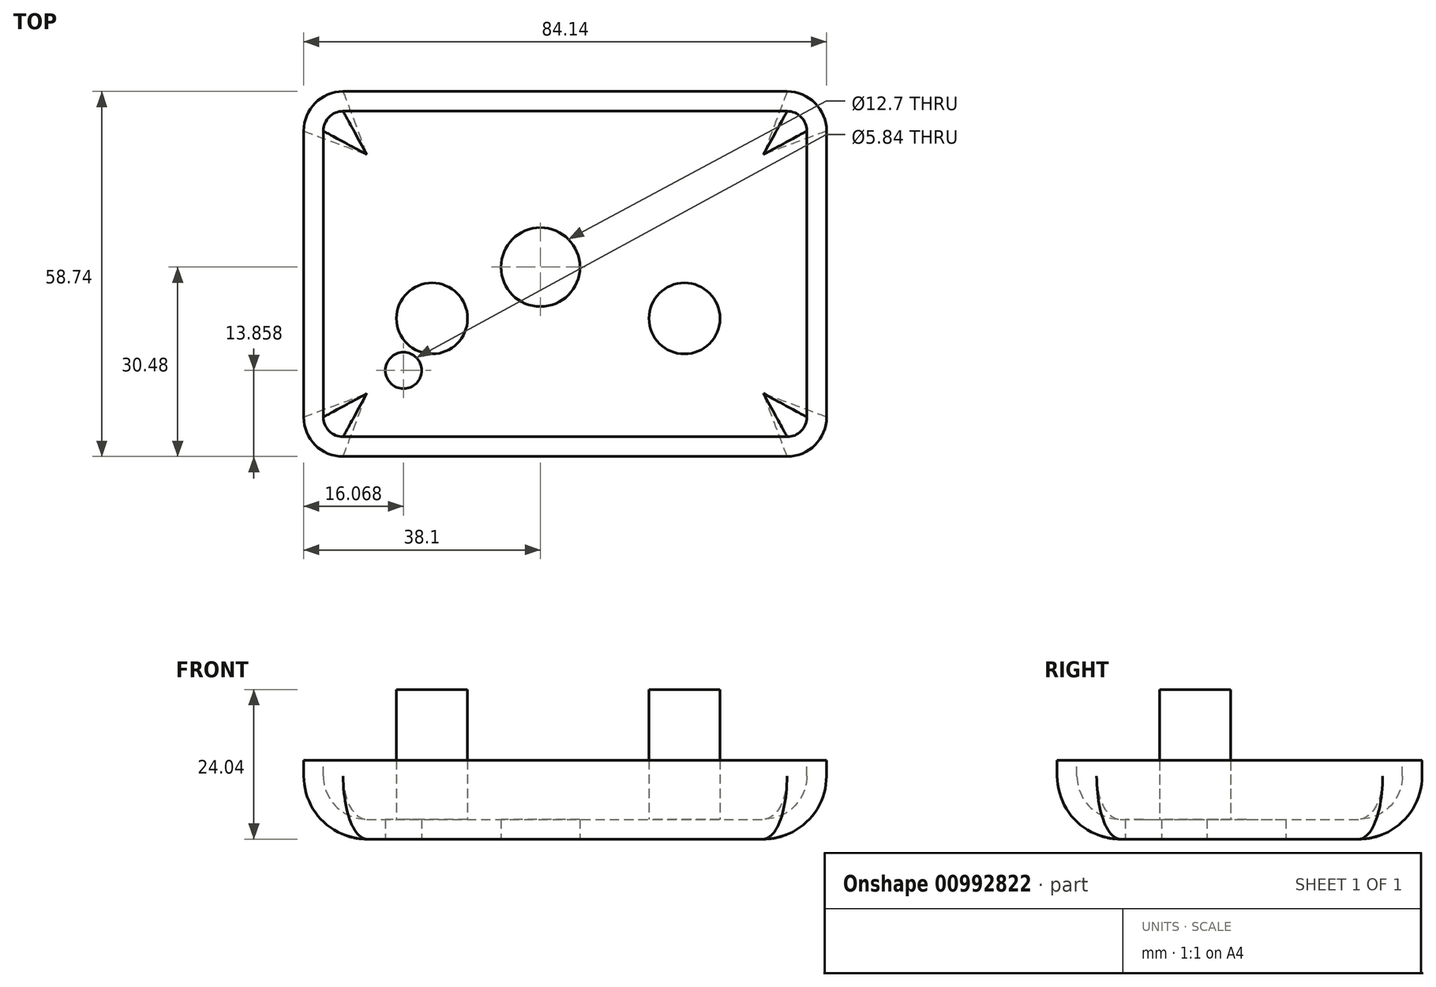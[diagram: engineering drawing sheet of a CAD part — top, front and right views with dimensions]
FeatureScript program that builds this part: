
annotation { "Feature Type Name" : "Feature", "Feature Type Description" : "" }
export const myFeature = defineFeature(function(context is Context, id is Id, definition is map)
    precondition{}
    {
        {
            var Q0;
            Q0=qCreatedBy(makeId("Top.planeOp"),FACE);
            var sketch = newSketch(context, id + "F0", { "sketchPlane" : qUnion([Q0])});
            skLineSegment(sketch, "E0.bottom", {"start": v(-31.75, 33.34) * mm, "end": v(39.69, 33.34) * mm});
            skLineSegment(sketch, "E0.top", {"start": v(-31.75, -25.4) * mm, "end": v(39.69, -25.4) * mm});
            skLineSegment(sketch, "E0.left", {"start": v(-38.1, 26.99) * mm, "end": v(-38.1, -19.05) * mm});
            skLineSegment(sketch, "E0.right", {"start": v(46.04, 26.99) * mm, "end": v(46.04, -19.05) * mm});
            skPoint(sketch, "E1.visualSharp", {"position": v(-38.1, -25.4) * mm});
            skArc(sketch, "E1.filletArc", {"start": v(-38.1, -19.05) * mm, "mid": v(-36.24, -23.54) * mm, "end": v(-31.75, -25.4) * mm});
            skPoint(sketch, "E2.visualSharp", {"position": v(-38.1, 33.34) * mm});
            skArc(sketch, "E2.filletArc", {"start": v(-31.75, 33.34) * mm, "mid": v(-36.24, 31.48) * mm, "end": v(-38.1, 26.99) * mm});
            skPoint(sketch, "E3.visualSharp", {"position": v(46.04, 33.34) * mm});
            skArc(sketch, "E3.filletArc", {"start": v(46.04, 26.99) * mm, "mid": v(44.18, 31.48) * mm, "end": v(39.69, 33.34) * mm});
            skPoint(sketch, "E4.visualSharp", {"position": v(46.04, -25.4) * mm});
            skArc(sketch, "E4.filletArc", {"start": v(39.69, -25.4) * mm, "mid": v(44.18, -23.54) * mm, "end": v(46.04, -19.05) * mm});
            skSolve(sketch);
        }
        {
            var Q0;
            Q0=makeQuery(id+"F0.imprint","IMPRINT",FACE,{"disambiguationData":[TD([[makeQuery(id+"F0.imprint","IMPRINT",EDGE,{"derivedFrom":sQuery(id+"F0.wireOp",EDGE,"E0.bottom")}),-1.0]])]});
            extrude(context, id + "F1", {"entities" : qUnion([Q0]), "oppositeDirection" : true, "depth" : 12.7 * mm, "offsetDistance" : 25.4 * mm});
        }
        {
            var Q0;
            Q0=makeQuery(id+"F1.opExtrude","CAP_EDGE",EDGE,{"disambiguationData":[OSD([sQuery(id+"F0.wireOp",EDGE,"E0.top")])],"isStart":false});
            var Q1;
            Q1=makeQuery(id+"F1.opExtrude","CAP_EDGE",EDGE,{"disambiguationData":[OSD([sQuery(id+"F0.wireOp",EDGE,"E1.filletArc")])],"isStart":false});
            var Q2;
            Q2=makeQuery(id+"F1.opExtrude","CAP_EDGE",EDGE,{"disambiguationData":[OSD([sQuery(id+"F0.wireOp",EDGE,"E0.left")])],"isStart":false});
            var Q3;
            Q3=makeQuery(id+"F1.opExtrude","CAP_EDGE",EDGE,{"disambiguationData":[OSD([sQuery(id+"F0.wireOp",EDGE,"E2.filletArc")])],"isStart":false});
            var Q4;
            Q4=makeQuery(id+"F1.opExtrude","CAP_EDGE",EDGE,{"disambiguationData":[OSD([sQuery(id+"F0.wireOp",EDGE,"E0.bottom")])],"isStart":false});
            var Q5;
            Q5=makeQuery(id+"F1.opExtrude","CAP_EDGE",EDGE,{"disambiguationData":[OSD([sQuery(id+"F0.wireOp",EDGE,"E3.filletArc")])],"isStart":false});
            var Q6;
            Q6=makeQuery(id+"F1.opExtrude","CAP_EDGE",EDGE,{"disambiguationData":[OSD([sQuery(id+"F0.wireOp",EDGE,"E0.right")])],"isStart":false});
            var Q7;
            Q7=makeQuery(id+"F1.opExtrude","CAP_EDGE",EDGE,{"disambiguationData":[OSD([sQuery(id+"F0.wireOp",EDGE,"E4.filletArc")])],"isStart":false});
            fillet(context, id + "F2", {"entities" : qUnion([Q0, Q1, Q2, Q3, Q4, Q5, Q6, Q7]), "radius" : 10.16 * mm, "tangentPropagation" : true, "allowEdgeOverflow" : false});
        }
        {
            var Q0;
            Q0=makeQuery(id+"F1.opExtrude","CAP_FACE",FACE,{"disambiguationData":[OSD([sQuery(id+"F0.wireOp",EDGE,"E0.bottom"),sQuery(id+"F0.wireOp",EDGE,"E0.top"),sQuery(id+"F0.wireOp",EDGE,"E0.left"),sQuery(id+"F0.wireOp",EDGE,"E0.right"),sQuery(id+"F0.wireOp",EDGE,"E1.filletArc"),sQuery(id+"F0.wireOp",EDGE,"E2.filletArc"),sQuery(id+"F0.wireOp",EDGE,"E3.filletArc"),sQuery(id+"F0.wireOp",EDGE,"E4.filletArc")])],"isStart":true});
            shell(context, id + "F3", {"entities" : qUnion([Q0]), "thickness" : 3.17 * mm});
        }
        {
            var Q0;
            Q0=makeQuery(id+"F3.opShell","OFFSET_FACE",FACE,{"disambiguationData":[OSD([sQuery(id+"F0.wireOp",EDGE,"E0.bottom"),sQuery(id+"F0.wireOp",EDGE,"E0.top"),sQuery(id+"F0.wireOp",EDGE,"E0.left"),sQuery(id+"F0.wireOp",EDGE,"E0.right"),sQuery(id+"F0.wireOp",EDGE,"E1.filletArc"),sQuery(id+"F0.wireOp",EDGE,"E2.filletArc"),sQuery(id+"F0.wireOp",EDGE,"E3.filletArc"),sQuery(id+"F0.wireOp",EDGE,"E4.filletArc")])]});
            var sketch = newSketch(context, id + "F4", { "sketchPlane" : qUnion([Q0])});
            skCircle(sketch, "E5", {"center": v(23.18, -3.17) * mm, "radius": 5.72 * mm});
            skCircle(sketch, "E6", {"center": v(-17.44, -3.18) * mm, "radius": 5.72 * mm});
            skSolve(sketch);
        }
        {
            var Q0;
            Q0 = qSketchRegion(id + "F4", true);
            extrude(context, id + "F5", {"entities" : qUnion([Q0]), "operationType" : NewBodyOperationType.ADD, "depth" : 20.87 * mm, "offsetDistance" : 25.4 * mm});
        }
        {
            var Q0;
            Q0=makeQuery(id+"F1.opExtrude","CAP_FACE",FACE,{"disambiguationData":[OSD([sQuery(id+"F0.wireOp",EDGE,"E0.bottom"),sQuery(id+"F0.wireOp",EDGE,"E0.top"),sQuery(id+"F0.wireOp",EDGE,"E0.left"),sQuery(id+"F0.wireOp",EDGE,"E0.right"),sQuery(id+"F0.wireOp",EDGE,"E1.filletArc"),sQuery(id+"F0.wireOp",EDGE,"E2.filletArc"),sQuery(id+"F0.wireOp",EDGE,"E3.filletArc"),sQuery(id+"F0.wireOp",EDGE,"E4.filletArc")])],"isStart":false});
            var sketch = newSketch(context, id + "F6", { "sketchPlane" : qUnion([Q0])});
            skCircle(sketch, "E7", {"center": v(0, -5.08) * mm, "radius": 5.08 * mm});
            skSolve(sketch);
        }
        {
            var Q0;
            Q0=sQuery(id+"F6.wireOp",VERTEX,"E7.center");
            var Q1;
            Q1=makeQuery(id+"F1.opExtrude","SWEPT_BODY",BODY,{"disambiguationData":[OSD([sQuery(id+"F0.wireOp",EDGE,"E0.bottom"),sQuery(id+"F0.wireOp",EDGE,"E0.top"),sQuery(id+"F0.wireOp",EDGE,"E0.left"),sQuery(id+"F0.wireOp",EDGE,"E0.right"),sQuery(id+"F0.wireOp",EDGE,"E1.filletArc"),sQuery(id+"F0.wireOp",EDGE,"E2.filletArc"),sQuery(id+"F0.wireOp",EDGE,"E3.filletArc"),sQuery(id+"F0.wireOp",EDGE,"E4.filletArc")])]});
            hole(context, id + "F7", {"style" : HoleStyle.SIMPLE, "endStyle" : HoleEndStyle.THROUGH, "holeDiameter" : 12.7 * mm, "majorDiameter" : 6.35 * mm, "isTappedThrough" : true, "tappedDepth" : 12.7 * mm, "tapClearance" : 3, "locations" : qUnion([Q0]), "scope" : qUnion([Q1])});
        }
        {
            var Q0;
            Q0=makeQuery(id+"F1.opExtrude","CAP_FACE",FACE,{"disambiguationData":[OSD([sQuery(id+"F0.wireOp",EDGE,"E0.bottom"),sQuery(id+"F0.wireOp",EDGE,"E0.top"),sQuery(id+"F0.wireOp",EDGE,"E0.left"),sQuery(id+"F0.wireOp",EDGE,"E0.right"),sQuery(id+"F0.wireOp",EDGE,"E1.filletArc"),sQuery(id+"F0.wireOp",EDGE,"E2.filletArc"),sQuery(id+"F0.wireOp",EDGE,"E3.filletArc"),sQuery(id+"F0.wireOp",EDGE,"E4.filletArc")])],"isStart":false});
            var sketch = newSketch(context, id + "F8", { "sketchPlane" : qUnion([Q0])});
            skCircle(sketch, "E8", {"center": v(-22.03, 11.54) * mm, "radius": 2.98 * mm});
            skSolve(sketch);
        }
        {
            var Q0;
            Q0=sQuery(id+"F8.wireOp",VERTEX,"E8.center");
            var Q1;
            Q1=makeQuery(id+"F1.opExtrude","SWEPT_BODY",BODY,{"disambiguationData":[OSD([sQuery(id+"F0.wireOp",EDGE,"E0.bottom"),sQuery(id+"F0.wireOp",EDGE,"E0.top"),sQuery(id+"F0.wireOp",EDGE,"E0.left"),sQuery(id+"F0.wireOp",EDGE,"E0.right"),sQuery(id+"F0.wireOp",EDGE,"E1.filletArc"),sQuery(id+"F0.wireOp",EDGE,"E2.filletArc"),sQuery(id+"F0.wireOp",EDGE,"E3.filletArc"),sQuery(id+"F0.wireOp",EDGE,"E4.filletArc")])]});
            hole(context, id + "F9", {"style" : HoleStyle.SIMPLE, "endStyle" : HoleEndStyle.THROUGH, "holeDiameter" : 5.84 * mm, "majorDiameter" : 6.35 * mm, "isTappedThrough" : true, "tappedDepth" : 12.7 * mm, "tapClearance" : 3, "locations" : qUnion([Q0]), "scope" : qUnion([Q1])});
        }
    });
